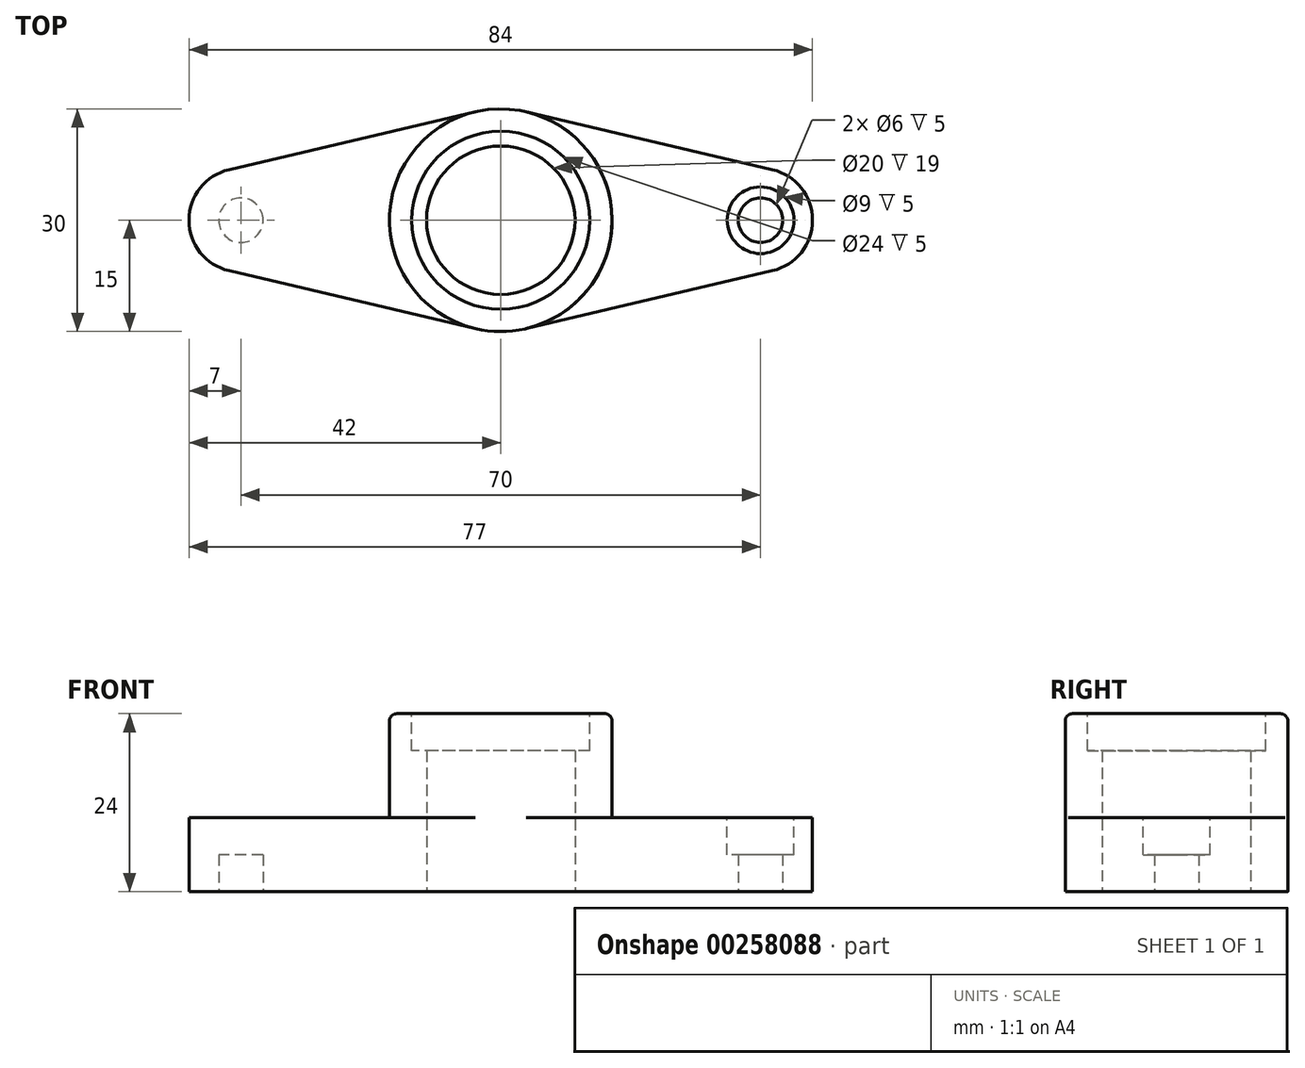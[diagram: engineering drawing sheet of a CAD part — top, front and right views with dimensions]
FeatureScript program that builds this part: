
annotation { "Feature Type Name" : "Feature", "Feature Type Description" : "" }
export const myFeature = defineFeature(function(context is Context, id is Id, definition is map)
    precondition{}
    {
        {
            var Q0;
            Q0=qCreatedBy(makeId("Top.planeOp"),FACE);
            var sketch = newSketch(context, id + "F0", { "sketchPlane" : qUnion([Q0])});
            skCircle(sketch, "E0", {"center": v(0, 0) * mm, "radius": 10 * mm});
            skCircle(sketch, "E1", {"center": v(0, 0) * mm, "radius": 15 * mm});
            skLineSegment(sketch, "E2", {"start": v(35, 0) * mm, "end": v(-35, 0) * mm, "construction": true});
            skCircle(sketch, "E3", {"center": v(35, 0) * mm, "radius": 7 * mm});
            skCircle(sketch, "E4", {"center": v(-35, 0) * mm, "radius": 7 * mm});
            skLineSegment(sketch, "E5", {"start": v(-36.6, 6.81) * mm, "end": v(-3.43, 14.6) * mm});
            skLineSegment(sketch, "E6", {"start": v(-3.43, -14.6) * mm, "end": v(-36.6, -6.81) * mm});
            skLineSegment(sketch, "E7", {"start": v(0, 47.53) * mm, "end": v(0, -35.4) * mm, "construction": true});
            skLineSegment(sketch, "E8.MirrorCS", {"start": v(65.63, 0) * mm, "end": v(36.6, 6.81) * mm});
            skLineSegment(sketch, "E9.MirrorCS", {"start": v(3.43, -14.6) * mm, "end": v(36.6, -6.81) * mm});
            skPoint(sketch, "E10.orphan", {"position": v(-4.64, 14.32) * mm});
            skPoint(sketch, "E11.orphan", {"position": v(4.64, 14.32) * mm});
            skPoint(sketch, "E12.orphan", {"position": v(5.67, -14.08) * mm});
            skPoint(sketch, "E13.orphan", {"position": v(-5.67, -14.08) * mm});
            skLineSegment(sketch, "E14.MirrorCS", {"start": v(3.43, 14.6) * mm, "end": v(36.6, 6.81) * mm});
            skSolve(sketch);
        }
        {
            var Q0;
            {var subQ0=sQuery(id+"F0.wireOp",EDGE,"E3");var subQ1=makeQuery(id+"F0.imprint","INTERSECT",VERTEX,{"derivedFrom":[subQ0,sQuery(id+"F0.wireOp",EDGE,"E14.MirrorCS")]});Q0=makeQuery(id+"F0.imprint","IMPRINT",FACE,{"disambiguationData":[TD([[makeQuery(id+"F0.imprint","IMPRINT",EDGE,{"disambiguationData":[TD([[subQ1,-1.0]])],"derivedFrom":subQ0}),1.0]])]});}
            var Q1;
            {var subQ0=sQuery(id+"F0.wireOp",EDGE,"E4");var subQ1=makeQuery(id+"F0.imprint","INTERSECT",VERTEX,{"derivedFrom":[subQ0,sQuery(id+"F0.wireOp",EDGE,"E5")]});Q1=makeQuery(id+"F0.imprint","IMPRINT",FACE,{"disambiguationData":[TD([[makeQuery(id+"F0.imprint","IMPRINT",EDGE,{"disambiguationData":[TD([[subQ1,-1.0]])],"derivedFrom":subQ0}),1.0]])]});}
            var Q2;
            {var subQ0=sQuery(id+"F0.wireOp",EDGE,"E9.MirrorCS");Q2=makeQuery(id+"F0.imprint","IMPRINT",FACE,{"disambiguationData":[TD([[makeQuery(id+"F0.imprint","IMPRINT",EDGE,{"derivedFrom":subQ0}),1.0]])]});}
            var Q3;
            Q3=makeQuery(id+"F0.imprint","IMPRINT",FACE,{"disambiguationData":[TD([[makeQuery(id+"F0.imprint","IMPRINT",EDGE,{"derivedFrom":sQuery(id+"F0.wireOp",EDGE,"E0")}),-1.0]])]});
            var Q4;
            {var subQ0=sQuery(id+"F0.wireOp",EDGE,"E5");Q4=makeQuery(id+"F0.imprint","IMPRINT",FACE,{"disambiguationData":[TD([[makeQuery(id+"F0.imprint","IMPRINT",EDGE,{"derivedFrom":subQ0}),-1.0]])]});}
            extrude(context, id + "F1", {"entities" : qUnion([Q0, Q1, Q2, Q3, Q4]), "depth" : 10 * mm});
        }
        {
            var Q0;
            Q0=makeQuery(id+"F1.opExtrude","CAP_FACE",FACE,{"disambiguationData":[OSD([sQuery(id+"F0.wireOp",EDGE,"E0"),sQuery(id+"F0.wireOp",EDGE,"E1"),sQuery(id+"F0.wireOp",EDGE,"E3"),sQuery(id+"F0.wireOp",EDGE,"E4"),sQuery(id+"F0.wireOp",EDGE,"E5"),sQuery(id+"F0.wireOp",EDGE,"E6"),sQuery(id+"F0.wireOp",EDGE,"E9.MirrorCS"),sQuery(id+"F0.wireOp",EDGE,"E14.MirrorCS")])],"isStart":false});
            var sketch = newSketch(context, id + "F2", { "sketchPlane" : qUnion([Q0])});
            skCircle(sketch, "E15", {"center": v(0, 0) * mm, "radius": 15 * mm});
            skCircle(sketch, "E16", {"center": v(0, 0) * mm, "radius": 10 * mm});
            skSolve(sketch);
        }
        {
            var Q0;
            Q0 = qSketchRegion(id + "F2", true);
            var Q1;
            Q1=makeQuery(id+"F2.imprint","IMPRINT",FACE,{"disambiguationData":[TD([[makeQuery(id+"F2.imprint","IMPRINT",EDGE,{"derivedFrom":sQuery(id+"F2.wireOp",EDGE,"E16")}),-1.0]])]});
            extrude(context, id + "F3", {"entities" : qUnion([Q0, Q1]), "operationType" : NewBodyOperationType.ADD, "depth" : 14 * mm});
        }
        {
            var Q0;
            Q0=qCreatedBy(makeId("Top.planeOp"),FACE);
            var sketch = newSketch(context, id + "F4", { "sketchPlane" : qUnion([Q0])});
            skCircle(sketch, "E17", {"center": v(35, 0) * mm, "radius": 3 * mm});
            skLineSegment(sketch, "E18", {"start": v(0, -38.98) * mm, "end": v(0, 19.97) * mm});
            skCircle(sketch, "E19.MirrorC", {"center": v(-35, 0) * mm, "radius": 3 * mm});
            skSolve(sketch);
        }
        {
            var Q0;
            Q0 = qSketchRegion(id + "F4", true);
            extrude(context, id + "F5", {"entities" : qUnion([Q0]), "operationType" : NewBodyOperationType.REMOVE, "depth" : 5 * mm});
        }
        {
            var Q0;
            {var subQ0=sQuery(id+"F0.wireOp",EDGE,"E3");var subQ1=sQuery(id+"F0.wireOp",EDGE,"E6");var subQ2=sQuery(id+"F0.wireOp",EDGE,"E1");var subQ3=sQuery(id+"F0.wireOp",EDGE,"E9.MirrorCS");var subQ4=sQuery(id+"F0.wireOp",EDGE,"E5");var subQ5=sQuery(id+"F0.wireOp",EDGE,"E14.MirrorCS");Q0=makeQuery(id+"F3.boolean.opBoolean","SPLIT",FACE,{"disambiguationData":[TD([makeQuery(id+"F1.opExtrude","SWEPT_FACE",FACE,{"disambiguationData":[OSD([subQ0])]})])],"derivedFrom":makeQuery(id+"F1.opExtrude","CAP_FACE",FACE,{"disambiguationData":[OSD([sQuery(id+"F0.wireOp",EDGE,"E0"),subQ2,subQ0,sQuery(id+"F0.wireOp",EDGE,"E4"),subQ4,subQ1,subQ3,subQ5])],"isStart":false})});}
            var sketch = newSketch(context, id + "F6", { "sketchPlane" : qUnion([Q0])});
            skCircle(sketch, "E20", {"center": v(35, 0) * mm, "radius": 4.5 * mm});
            skLineSegment(sketch, "E21", {"start": v(0, -30.6) * mm, "end": v(0, 29.76) * mm});
            skCircle(sketch, "E22.MirrorC", {"center": v(-35, 0) * mm, "radius": 4.5 * mm});
            skSolve(sketch);
        }
        {
            var Q0;
            Q0=makeQuery(id+"F6.imprint","IMPRINT",FACE,{"disambiguationData":[TD([[makeQuery(id+"F6.imprint","IMPRINT",EDGE,{"derivedFrom":sQuery(id+"F6.wireOp",EDGE,"E20")}),1.0]])]});
            var Q1;
            Q1=makeQuery(id+"F6.imprint","IMPRINT",FACE,{"disambiguationData":[TD([[makeQuery(id+"F6.imprint","IMPRINT",EDGE,{"derivedFrom":sQuery(id+"F6.wireOp",EDGE,"E22.MirrorC")}),-1.0]])]});
            extrude(context, id + "F7", {"entities" : qUnion([Q0, Q1]), "operationType" : NewBodyOperationType.REMOVE, "oppositeDirection" : true, "depth" : 5 * mm});
        }
        {
            var Q0;
            Q0=makeQuery(id+"F3.opExtrude","CAP_FACE",FACE,{"disambiguationData":[OSD([sQuery(id+"F2.wireOp",EDGE,"E15"),sQuery(id+"F2.wireOp",EDGE,"E16")])],"isStart":false});
            var sketch = newSketch(context, id + "F8", { "sketchPlane" : qUnion([Q0])});
            skCircle(sketch, "E23", {"center": v(0, 0) * mm, "radius": 12 * mm});
            skSolve(sketch);
        }
        {
            var Q0;
            Q0 = qSketchRegion(id + "F8", true);
            extrude(context, id + "F9", {"entities" : qUnion([Q0]), "operationType" : NewBodyOperationType.REMOVE, "oppositeDirection" : true, "depth" : 5 * mm});
        }
        {
            var Q0;
            Q0=makeQuery(id+"F3.opExtrude","CAP_EDGE",EDGE,{"disambiguationData":[OSD([sQuery(id+"F2.wireOp",EDGE,"E15")])],"isStart":false});
            fillet(context, id + "F10", {"entities" : qUnion([Q0]), "radius" : 1 * mm, "tangentPropagation" : true, "allowEdgeOverflow" : false});
        }
    });
